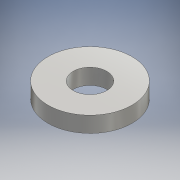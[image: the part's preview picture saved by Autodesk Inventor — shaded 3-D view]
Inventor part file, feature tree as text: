
AUTODESK INVENTOR PART (.ipt)
format: ipt  version: 2016 (Build 200138000, 138)  size: 97,280 bytes
history: native  units: mm
features: other x1, extrude x1, sketch x1
ambient origin geometry x8: Origin, YZ Plane, XZ Plane, XY Plane, X Axis, Y Axis, Z Axis, Center Point
bodies: Body1 (feature_tree)
feature tree (3):
  other  "ソリッド1"
  extrude  "押し出し1"  Depth=3.2mm
  sketch  "スケッチ1"
